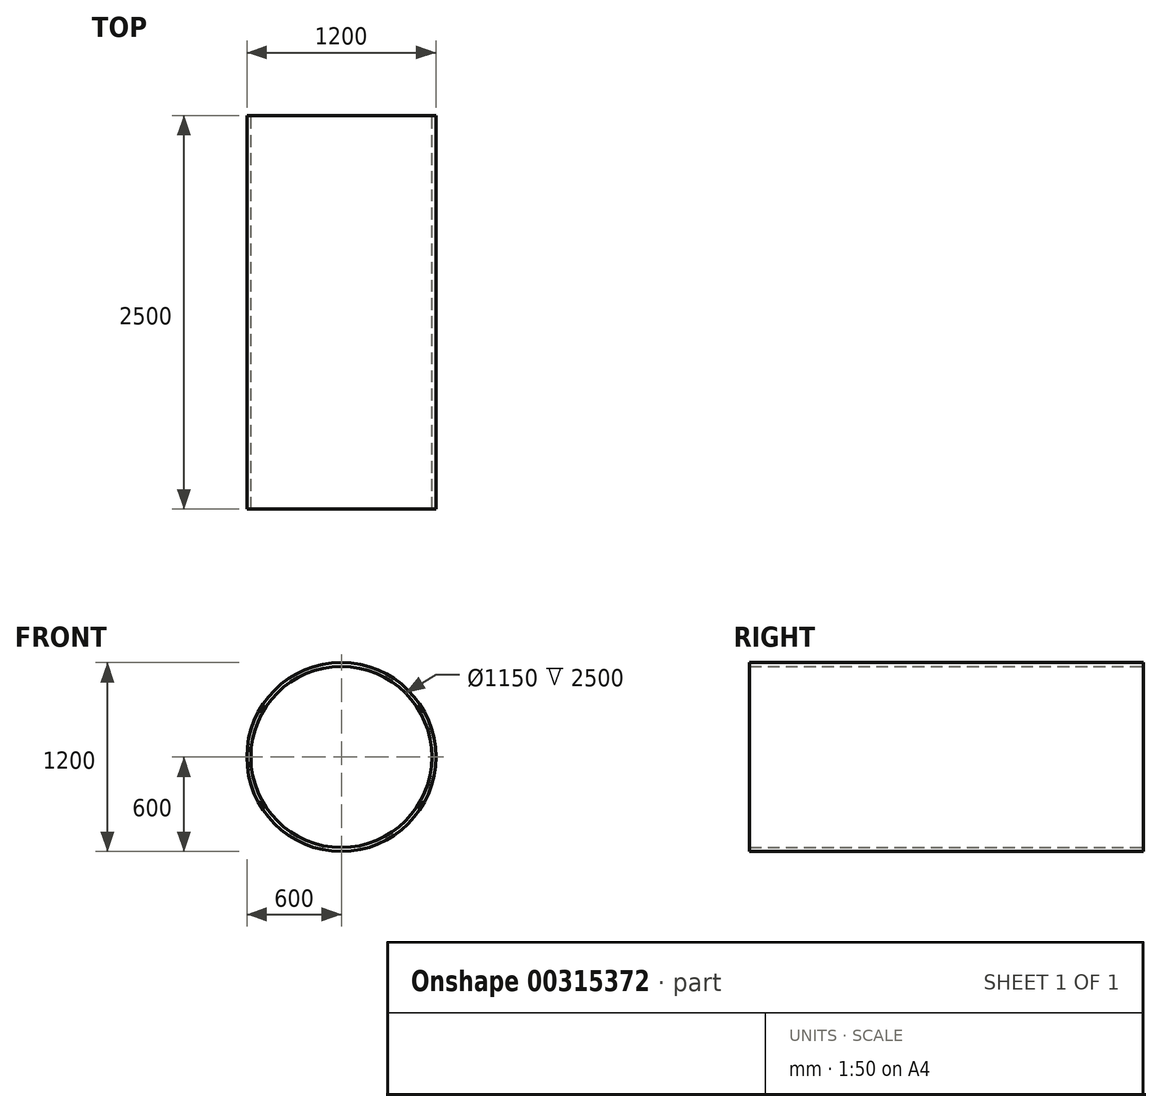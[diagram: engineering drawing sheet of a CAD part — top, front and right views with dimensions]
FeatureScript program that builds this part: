
annotation { "Feature Type Name" : "Feature", "Feature Type Description" : "" }
export const myFeature = defineFeature(function(context is Context, id is Id, definition is map)
    precondition{}
    {
        {
            var Q0;
            Q0=qCreatedBy(makeId("Front.planeOp"),FACE);
            var sketch = newSketch(context, id + "F0", { "sketchPlane" : qUnion([Q0])});
            skCircle(sketch, "E0", {"center": v(0, 0) * mm, "radius": 600 * mm});
            skCircle(sketch, "E1", {"center": v(0, 0) * mm, "radius": 575 * mm});
            skSolve(sketch);
        }
        {
            var Q0;
            Q0 = qSketchRegion(id + "F0", true);
            extrude(context, id + "F1", {"entities" : qUnion([Q0]), "depth" : 2500 * mm});
        }
    });
